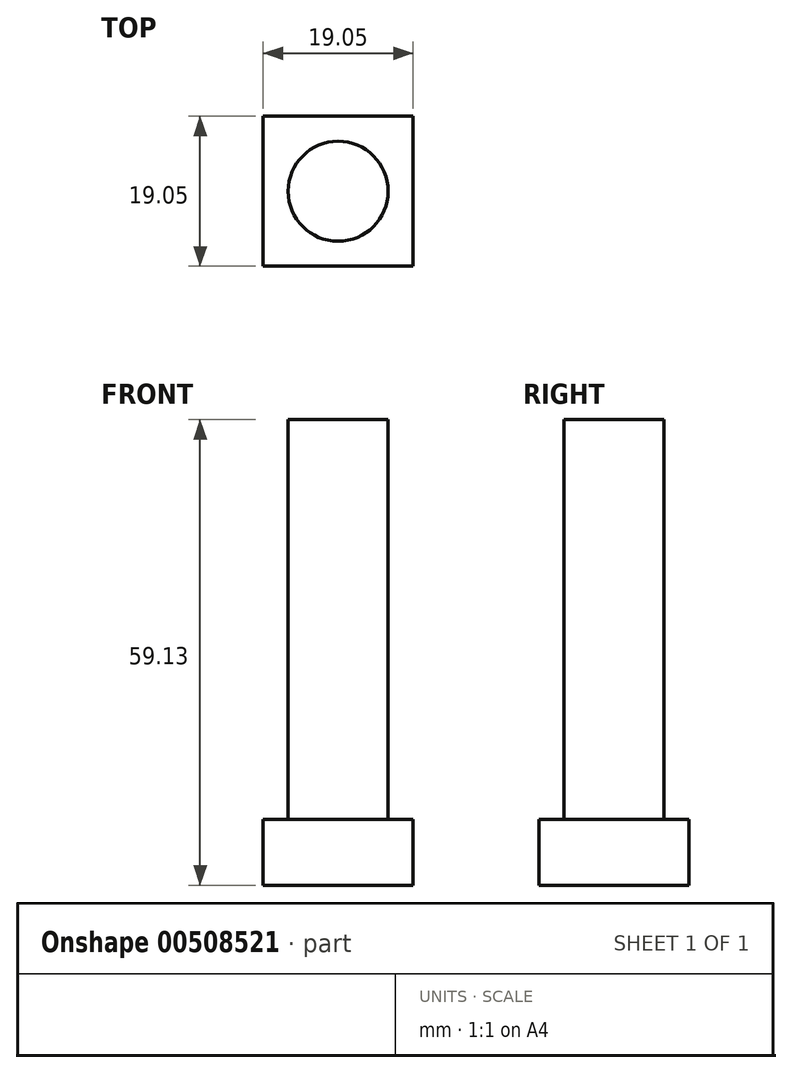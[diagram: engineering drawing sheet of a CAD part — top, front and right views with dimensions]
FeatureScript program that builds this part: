
annotation { "Feature Type Name" : "Feature", "Feature Type Description" : "" }
export const myFeature = defineFeature(function(context is Context, id is Id, definition is map)
    precondition{}
    {
        {
            var Q0;
            Q0=qCreatedBy(makeId("Top.planeOp"),FACE);
            var sketch = newSketch(context, id + "F0", { "sketchPlane" : qUnion([Q0])});
            skLineSegment(sketch, "E0.bottom", {"start": v(0, 0) * mm, "end": v(19.05, 0) * mm});
            skLineSegment(sketch, "E0.top", {"start": v(0, -19.05) * mm, "end": v(19.05, -19.05) * mm});
            skLineSegment(sketch, "E0.left", {"start": v(0, 0) * mm, "end": v(0, -19.05) * mm});
            skLineSegment(sketch, "E0.right", {"start": v(19.05, 0) * mm, "end": v(19.05, -19.05) * mm});
            skSolve(sketch);
        }
        {
            var Q0;
            Q0=makeQuery(id+"F0.imprint","IMPRINT",FACE,{"disambiguationData":[TD([[makeQuery(id+"F0.imprint","IMPRINT",EDGE,{"derivedFrom":sQuery(id+"F0.wireOp",EDGE,"E0.bottom")}),-1.0]])]});
            extrude(context, id + "F1", {"entities" : qUnion([Q0]), "depth" : 8.33 * mm, "offsetDistance" : 25.4 * mm});
        }
        {
            var Q0;
            Q0=makeQuery(id+"F1.opExtrude","CAP_FACE",FACE,{"disambiguationData":[OSD([sQuery(id+"F0.wireOp",EDGE,"E0.bottom"),sQuery(id+"F0.wireOp",EDGE,"E0.top"),sQuery(id+"F0.wireOp",EDGE,"E0.left"),sQuery(id+"F0.wireOp",EDGE,"E0.right")])],"isStart":false});
            var sketch = newSketch(context, id + "F2", { "sketchPlane" : qUnion([Q0])});
            skLineSegment(sketch, "E1", {"start": v(0, -9.53) * mm, "end": v(19.05, -9.53) * mm, "construction": true});
            skLineSegment(sketch, "E2", {"start": v(9.53, 0) * mm, "end": v(9.53, -19.05) * mm, "construction": true});
            skPoint(sketch, "E3", {"position": v(9.53, -9.53) * mm});
            skCircle(sketch, "E4", {"center": v(9.53, -9.53) * mm, "radius": 6.35 * mm});
            skSolve(sketch);
        }
        {
            var Q0;
            Q0=makeQuery(id+"F2.imprint","IMPRINT",FACE,{"disambiguationData":[TD([[makeQuery(id+"F2.imprint","IMPRINT",EDGE,{"derivedFrom":sQuery(id+"F2.wireOp",EDGE,"E4")}),1.0]])]});
            extrude(context, id + "F3", {"entities" : qUnion([Q0]), "operationType" : NewBodyOperationType.ADD, "depth" : 50.8 * mm, "offsetDistance" : 25.4 * mm});
        }
    });
